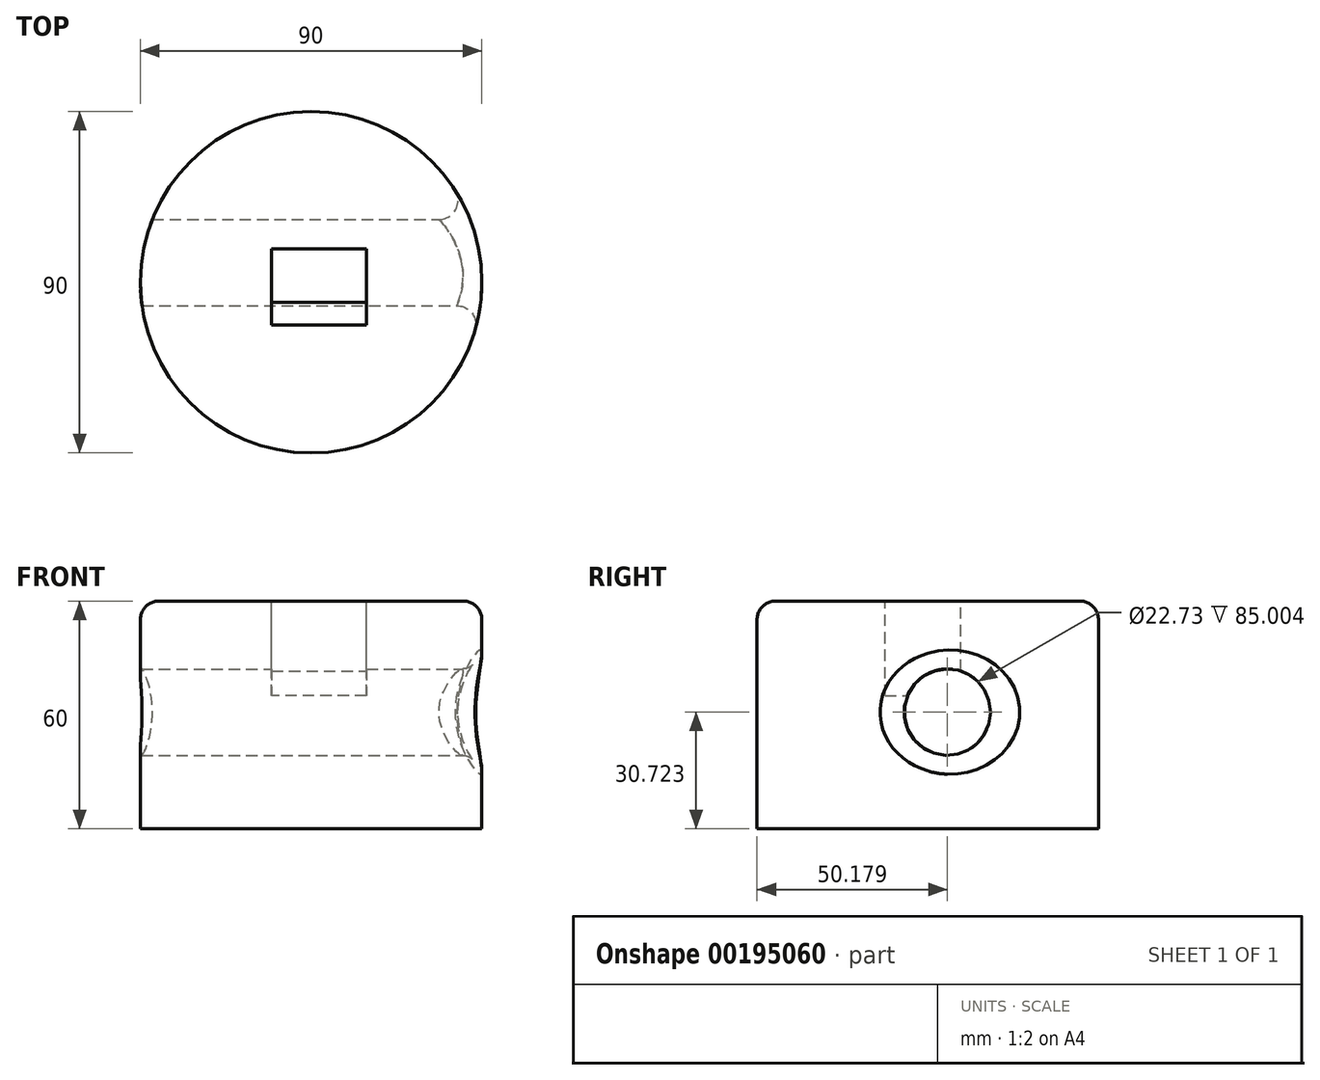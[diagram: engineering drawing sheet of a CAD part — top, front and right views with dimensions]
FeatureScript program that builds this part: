
annotation { "Feature Type Name" : "Feature", "Feature Type Description" : "" }
export const myFeature = defineFeature(function(context is Context, id is Id, definition is map)
    precondition{}
    {
        {
            var Q0;
            Q0=qCreatedBy(makeId("Top.planeOp"),FACE);
            var sketch = newSketch(context, id + "F0", { "sketchPlane" : qUnion([Q0])});
            skCircle(sketch, "E0", {"center": v(0, 0) * mm, "radius": 45 * mm});
            skSolve(sketch);
        }
        {
            var Q0;
            Q0=makeQuery(id+"F0.imprint","IMPRINT",FACE,{"disambiguationData":[TD([[makeQuery(id+"F0.imprint","IMPRINT",EDGE,{"derivedFrom":sQuery(id+"F0.wireOp",EDGE,"E0")}),1.0]])]});
            extrude(context, id + "F1", {"entities" : qUnion([Q0]), "depth" : 60 * mm});
        }
        {
            var Q0;
            Q0=makeQuery(id+"F1.opExtrude","CAP_FACE",FACE,{"disambiguationData":[OSD([sQuery(id+"F0.wireOp",EDGE,"E0")])],"isStart":false});
            var sketch = newSketch(context, id + "F2", { "sketchPlane" : qUnion([Q0])});
            skLineSegment(sketch, "E1.bottom", {"start": v(14.6, -11.28) * mm, "end": v(-10.4, -11.28) * mm});
            skLineSegment(sketch, "E1.top", {"start": v(14.6, 8.72) * mm, "end": v(-10.4, 8.72) * mm});
            skLineSegment(sketch, "E1.left", {"start": v(14.6, -11.28) * mm, "end": v(14.6, 8.72) * mm});
            skLineSegment(sketch, "E1.right", {"start": v(-10.4, -11.28) * mm, "end": v(-10.4, 8.72) * mm});
            skSolve(sketch);
        }
        {
            var Q0;
            Q0=makeQuery(id+"F2.imprint","IMPRINT",FACE,{"disambiguationData":[TD([[makeQuery(id+"F2.imprint","IMPRINT",EDGE,{"derivedFrom":sQuery(id+"F2.wireOp",EDGE,"E1.bottom")}),-1.0]])]});
            extrude(context, id + "F3", {"entities" : qUnion([Q0]), "operationType" : NewBodyOperationType.REMOVE, "oppositeDirection" : true, "depth" : 25 * mm});
        }
        {
            var Q0;
            Q0=qCreatedBy(makeId("Right.planeOp"),FACE);
            var sketch = newSketch(context, id + "F4", { "sketchPlane" : qUnion([Q0])});
            skCircle(sketch, "E2", {"center": v(5.18, 30.72) * mm, "radius": 11.36 * mm});
            skSolve(sketch);
        }
        {
            var Q0;
            Q0=makeQuery(id+"F4.imprint","IMPRINT",FACE,{"disambiguationData":[TD([[makeQuery(id+"F4.imprint","IMPRINT",EDGE,{"derivedFrom":sQuery(id+"F4.wireOp",EDGE,"E2")}),1.0]])]});
            extrude(context, id + "F5", {"entities" : qUnion([Q0]), "operationType" : NewBodyOperationType.REMOVE, "endBound" : BoundingType.SYMMETRIC, "oppositeDirection" : true, "depth" : 110 * mm});
        }
        {
            var Q0;
            Q0=makeQuery(id+"F5.boolean.opBoolean","INTERSECT",EDGE,{"disambiguationData":[OD(1.0)],"derivedFrom":[makeQuery(id+"F1.opExtrude","SWEPT_FACE",FACE,{"disambiguationData":[OSD([sQuery(id+"F0.wireOp",EDGE,"E0")])]}),makeQuery(id+"F5.opExtrude","SWEPT_FACE",FACE,{"disambiguationData":[OSD([sQuery(id+"F4.wireOp",EDGE,"E2")])]})]});
            var Q1;
            Q1=makeQuery(id+"F1.opExtrude","CAP_EDGE",EDGE,{"disambiguationData":[OSD([sQuery(id+"F0.wireOp",EDGE,"E0")])],"isStart":false});
            fillet(context, id + "F6", {"entities" : qUnion([Q0, Q1]), "radius" : 5 * mm, "tangentPropagation" : true, "allowEdgeOverflow" : false});
        }
    });
